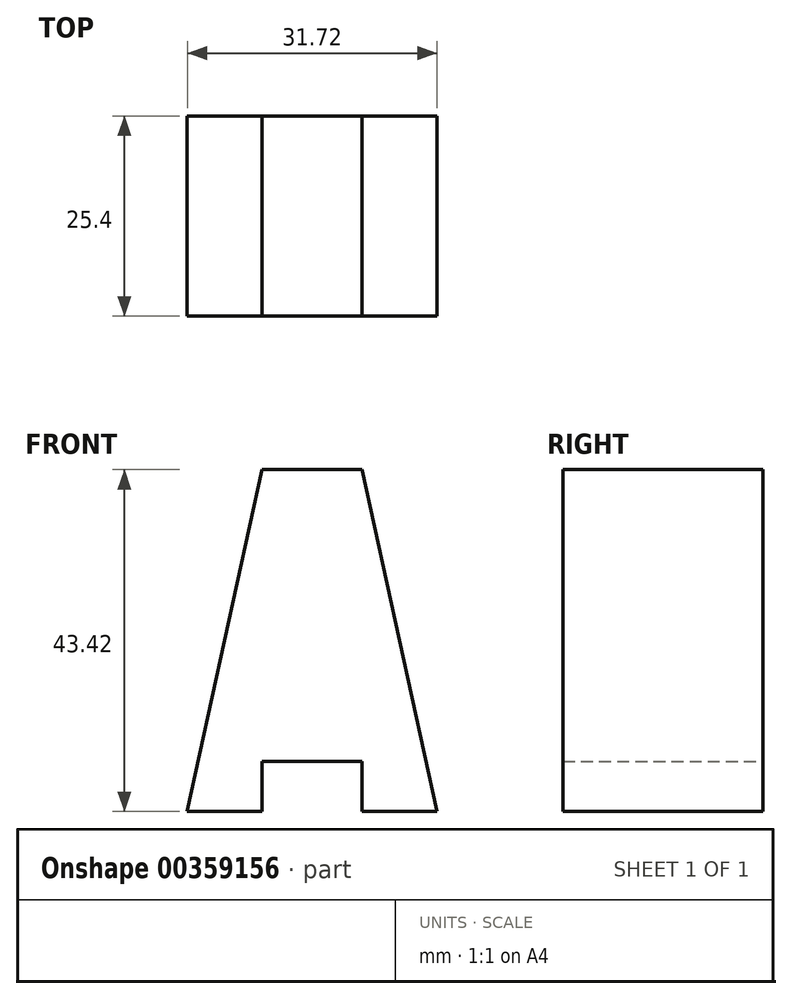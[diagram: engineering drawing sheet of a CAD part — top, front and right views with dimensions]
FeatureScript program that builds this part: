
annotation { "Feature Type Name" : "Feature", "Feature Type Description" : "" }
export const myFeature = defineFeature(function(context is Context, id is Id, definition is map)
    precondition{}
    {
        {
            var Q0;
            Q0=qCreatedBy(makeId("Front.planeOp"),FACE);
            var sketch = newSketch(context, id + "F0", { "sketchPlane" : qUnion([Q0])});
            skLineSegment(sketch, "E0", {"start": v(2.02, 0) * mm, "end": v(11.53, 43.42) * mm});
            skLineSegment(sketch, "E1", {"start": v(11.53, 43.42) * mm, "end": v(24.23, 43.42) * mm});
            skLineSegment(sketch, "E2", {"start": v(24.23, 43.42) * mm, "end": v(33.74, 0) * mm});
            skLineSegment(sketch, "E3", {"start": v(33.74, 0) * mm, "end": v(24.23, 0) * mm});
            skLineSegment(sketch, "E4", {"start": v(24.23, 0) * mm, "end": v(24.23, 6.35) * mm});
            skLineSegment(sketch, "E5", {"start": v(24.23, 6.35) * mm, "end": v(11.53, 6.35) * mm});
            skLineSegment(sketch, "E6", {"start": v(11.53, 6.35) * mm, "end": v(11.53, 0) * mm});
            skLineSegment(sketch, "E7", {"start": v(11.53, 0) * mm, "end": v(2.02, 0) * mm});
            skSolve(sketch);
        }
        {
            var Q0;
            Q0 = qSketchRegion(id + "F0", true);
            extrude(context, id + "F1", {"entities" : qUnion([Q0]), "depth" : 25.4 * mm});
        }
    });
